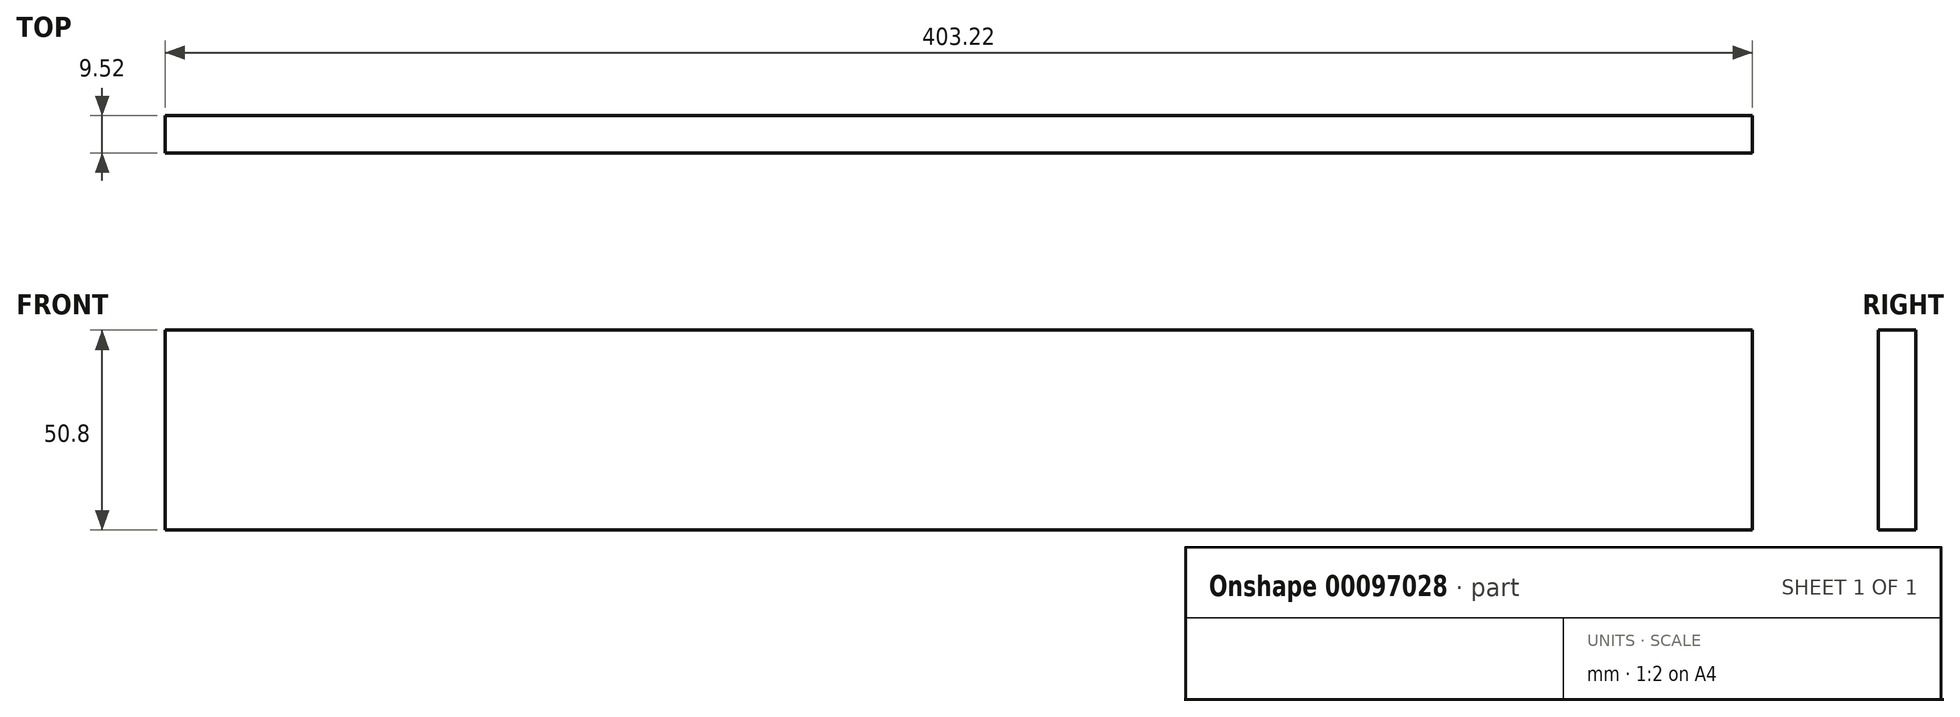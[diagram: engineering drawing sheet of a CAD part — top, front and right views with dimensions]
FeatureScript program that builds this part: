
annotation { "Feature Type Name" : "Feature", "Feature Type Description" : "" }
export const myFeature = defineFeature(function(context is Context, id is Id, definition is map)
    precondition{}
    {
        {
            var Q0;
            Q0=qCreatedBy(makeId("Front.planeOp"),FACE);
            var sketch = newSketch(context, id + "F0", { "sketchPlane" : qUnion([Q0])});
            skLineSegment(sketch, "E0.bottom", {"start": v(-201.61, 25.4) * mm, "end": v(201.61, 25.4) * mm});
            skLineSegment(sketch, "E0.top", {"start": v(-201.61, -25.4) * mm, "end": v(201.61, -25.4) * mm});
            skLineSegment(sketch, "E0.left", {"start": v(-201.61, 25.4) * mm, "end": v(-201.61, -25.4) * mm});
            skLineSegment(sketch, "E0.right", {"start": v(201.61, 25.4) * mm, "end": v(201.61, -25.4) * mm});
            skPoint(sketch, "E0.middle", {"position": v(0, 0) * mm});
            skSolve(sketch);
        }
        {
            var Q0;
            Q0 = qSketchRegion(id + "F0", true);
            extrude(context, id + "F1", {"entities" : qUnion([Q0]), "endBound" : BoundingType.SYMMETRIC, "depth" : 9.52 * mm});
        }
    });
